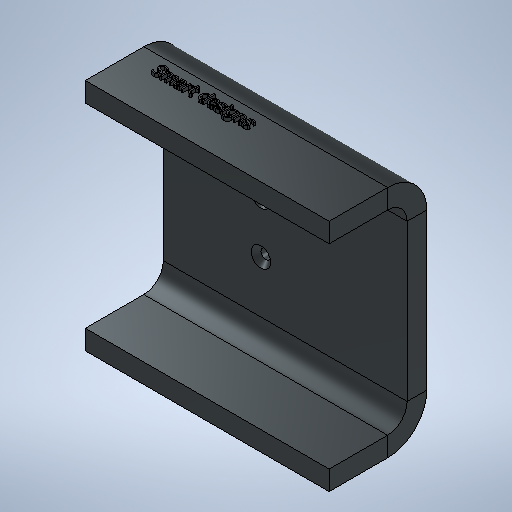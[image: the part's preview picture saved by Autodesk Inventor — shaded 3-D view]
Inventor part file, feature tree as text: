
AUTODESK INVENTOR PART (.ipt)
format: ipt  version: 2025 (Build 290162010, 162A)  size: 680,960 bytes
history: native  units: mm
features: other x6, sketch x4, hole x1, emboss x1, projected_geometry x1
ambient origin geometry x8: Origin, YZ Plane, XZ Plane, XY Plane, X Axis, Y Axis, Z Axis, Center Point
bodies: Volumenkörper3 (feature_tree)
feature tree (13):
  other  "Fläche2"
  other  "Lasche1"
  hole  "Bohrung2"  [1 undecoded]
  emboss  "Emboss1"
  sketch  "Skizze1"  dims[d0=75.0mm d1=60.0mm]
  other  "Grobblech2"
  sketch  "Skizze2"  dims[d5=6.0mm]
  other  "Grobblech3"
  other  "Biegung1"
  other  "Ecke1"
  sketch  "Skizze3"  dims[d6=6.0mm]
  projected_geometry  "Projizierte Kontur1"
  sketch  "Sketch4"  dims[d7=3.0mm d8=12.0mm d9=6.0mm d10=30.0mm d11=90.0deg d12=6.0mm d13=24.0mm d14=6.0mm d15=6.0mm d23=16.0mm d24=30.0mm d25=28.0mm d26=3.0mm d27=6.0mm d28=6.0mm d29=2.0mm d30=90.0deg d31=8.0mm d32=0.0mm d33=1.0mm d34=0.0mm]
note: 1 required parameter value undecoded (feature->parameter linkage not recoverable at this tier; creation-order binding heuristic only, values carry confidence <= 0.55)
